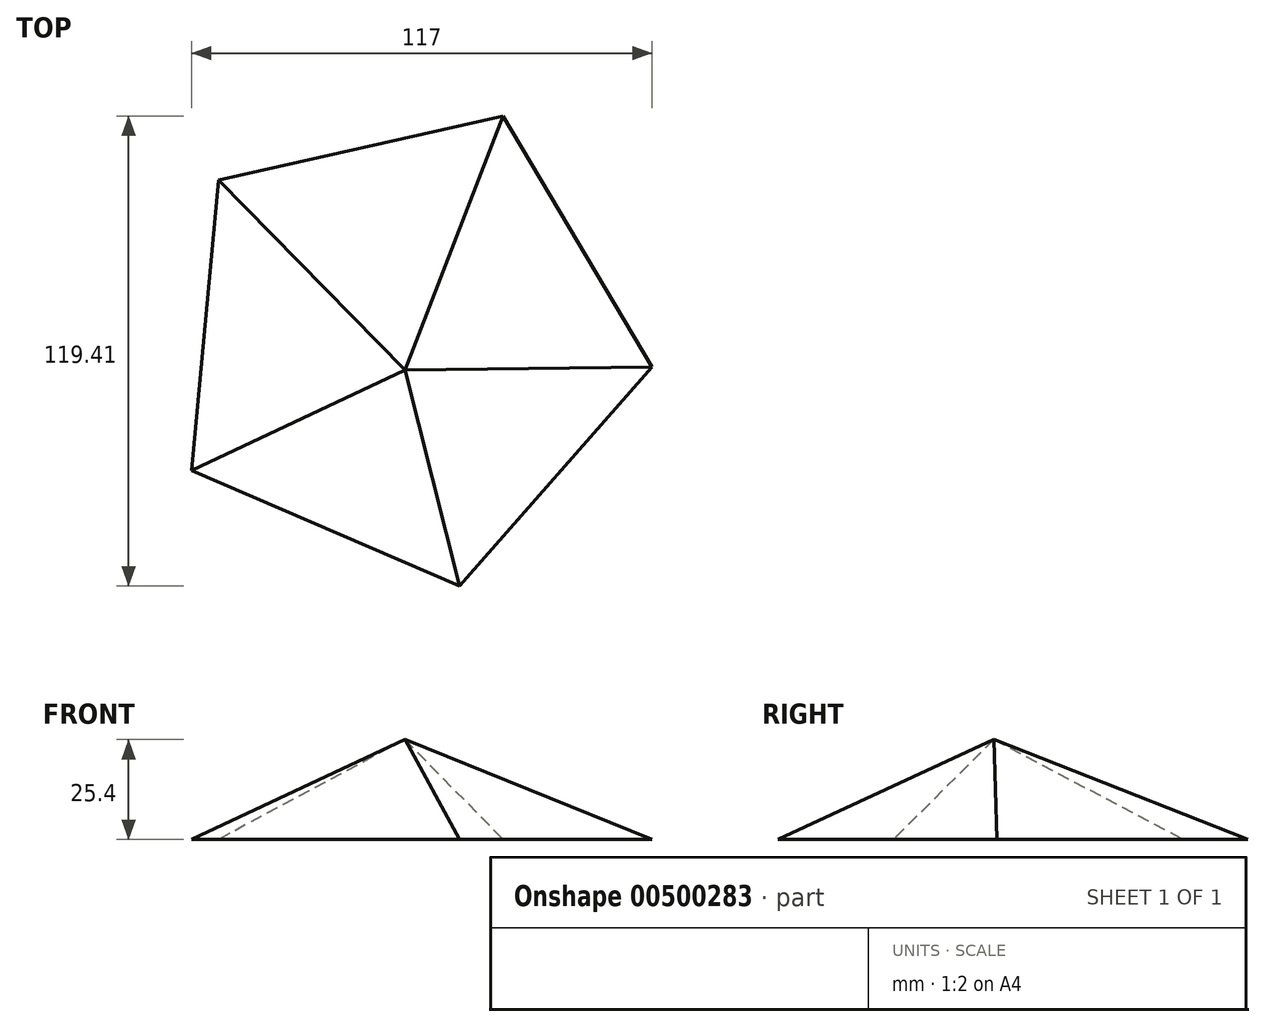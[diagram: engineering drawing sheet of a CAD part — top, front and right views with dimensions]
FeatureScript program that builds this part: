
annotation { "Feature Type Name" : "Feature", "Feature Type Description" : "" }
export const myFeature = defineFeature(function(context is Context, id is Id, definition is map)
    precondition{}
    {
        {
            var Q0;
            Q0=qCreatedBy(makeId("Top.planeOp"),FACE);
            var sketch = newSketch(context, id + "F0", { "sketchPlane" : qUnion([Q0])});
            skCircle(sketch, "E0.cCircle", {"center": v(0, 0) * mm, "radius": 63.05 * mm, "construction": true});
            skLineSegment(sketch, "E0.0", {"start": v(-47.36, 41.62) * mm, "end": v(24.95, 57.9) * mm});
            skLineSegment(sketch, "E0.1", {"start": v(24.95, 57.9) * mm, "end": v(62.78, -5.84) * mm});
            skLineSegment(sketch, "E0.2", {"start": v(62.78, -5.84) * mm, "end": v(13.85, -61.5) * mm});
            skLineSegment(sketch, "E0.3", {"start": v(13.85, -61.5) * mm, "end": v(-54.22, -32.18) * mm});
            skLineSegment(sketch, "E0.4", {"start": v(-54.22, -32.18) * mm, "end": v(-47.36, 41.62) * mm});
            skSolve(sketch);
        }
        {
            var Q0;
            Q0=qCreatedBy(makeId("Top.planeOp"),FACE);
            cPlane(context, id + "F1", {"entities" : qUnion([Q0]), "cplaneType" : CPlaneType.OFFSET, "offset" : 25.4 * mm, "width" : 152.4 * mm, "height" : 152.4 * mm});
        }
        {
            var Q0;
            Q0=qCreatedBy(id+"F1.planeOp",FACE);
            var sketch = newSketch(context, id + "F2", { "sketchPlane" : qUnion([Q0])});
            skLineSegment(sketch, "E1.bottom", {"start": v(-43.7, 36.77) * mm, "end": v(43.7, 36.77) * mm});
            skLineSegment(sketch, "E1.top", {"start": v(-43.7, -50.07) * mm, "end": v(43.7, -50.07) * mm});
            skLineSegment(sketch, "E1.left", {"start": v(-43.7, 36.77) * mm, "end": v(-43.7, -50.07) * mm});
            skLineSegment(sketch, "E1.right", {"start": v(43.7, 36.77) * mm, "end": v(43.7, -50.07) * mm});
            skPoint(sketch, "E1.middle", {"position": v(0, -6.65) * mm});
            skSolve(sketch);
        }
        {
            var Q0;
            Q0=sQuery(id+"F2.wireOp",VERTEX,"E1.middle");
            var Q1;
            Q1=makeQuery(id+"F0.imprint","IMPRINT",FACE,{"disambiguationData":[TD([[makeQuery(id+"F0.imprint","IMPRINT",EDGE,{"derivedFrom":sQuery(id+"F0.wireOp",EDGE,"E0.0")}),-1.0]])]});
            loft(context, id + "F3", {"sheetProfilesArray" : [{ "sheetProfileEntities" : qUnion([Q0]) }, { "sheetProfileEntities" : qUnion([Q1]) }]});
        }
    });
